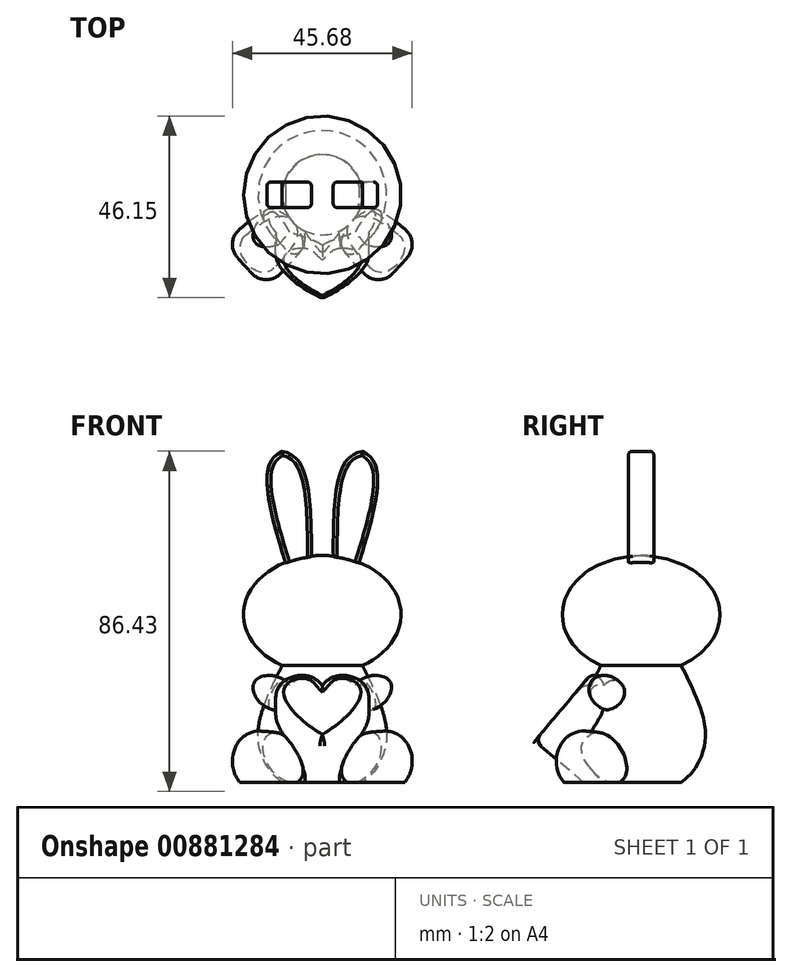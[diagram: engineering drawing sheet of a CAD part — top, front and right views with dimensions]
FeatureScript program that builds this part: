
annotation { "Feature Type Name" : "Feature", "Feature Type Description" : "" }
export const myFeature = defineFeature(function(context is Context, id is Id, definition is map)
    precondition{}
    {
        {
            var Q0;
            Q0=qCreatedBy(makeId("Front.planeOp"),FACE);
            var sketch = newSketch(context, id + "F0", { "sketchPlane" : qUnion([Q0])});
            skEllipticalArc(sketch, "E0", {});
            skLineSegment(sketch, "E1", {"start": v(0, 24.54) * mm, "end": v(0, -22.96) * mm, "construction": true});
            skLineSegment(sketch, "E2", {"start": v(0, 15) * mm, "end": v(0, -15) * mm});
            const initialGuessF0  = {"E0": [0, 0, -1, 0, 0.02, 0.015, 4.71238898038469, 1.5707963267948966]};
            skSetInitialGuess(sketch, initialGuessF0);
            skSolve(sketch);
        }
        {
            var Q0;
            Q0=makeQuery(id+"F0.imprint","IMPRINT",FACE,{"disambiguationData":[TD([[makeQuery(id+"F0.imprint","IMPRINT",EDGE,{"derivedFrom":sQuery(id+"F0.wireOp",EDGE,"E0")}),1.0]])]});
            var Q1;
            Q1=sQuery(id+"F0.wireOp",EDGE,"E1");
            revolve(context, id + "F1", {"surfaceOperationType" : NewSurfaceOperationType.NEW, "entities" : qUnion([Q0]), "axis" : qUnion([Q1]), "revolveType" : RevolveType.FULL});
        }
        {
            var Q0;
            Q0=qCreatedBy(makeId("Front.planeOp"),FACE);
            var sketch = newSketch(context, id + "F2", { "sketchPlane" : qUnion([Q0])});
            skLineSegment(sketch, "E3", {"start": v(-4, 0) * mm, "end": v(-10.24, 41.49) * mm, "construction": true});
            skLineSegment(sketch, "E4", {"start": v(-4, 0) * mm, "end": v(-4, 44.56) * mm, "construction": true});
            skFitSpline(sketch, "E5", {"points": [v(-8.8, 11.5) * mm, v(-13.75, 30.32) * mm, v(-13.13, 38.8) * mm, v(-10.24, 41.49) * mm], "startDerivative": vector(-13.36, 42.4) * mm, "endDerivative": vector(15.53, 10.02) * mm});
            skFitSpline(sketch, "E6.MirrorCS", {"points": [v(-2.8, 12.4) * mm, v(-3.6, 31.85) * mm, v(-6.68, 39.77) * mm, v(-10.24, 41.49) * mm], "startDerivative": vector(0.3, 44.46) * mm, "endDerivative": vector(-17.79, 5) * mm});
            skLineSegment(sketch, "E7", {"start": v(-8.8, 11.5) * mm, "end": v(-2.8, 12.4) * mm});
            skSolve(sketch);
        }
        {
            var Q0;
            {var subQ5=sQuery(id+"F2.wireOp",EDGE,"E5");Q0=makeQuery(id+"F2.imprint","IMPRINT",FACE,{"disambiguationData":[TD([[makeQuery(id+"F2.imprint","IMPRINT",EDGE,{"derivedFrom":subQ5}),-1.0]])]});}
            extrude(context, id + "F3", {"entities" : qUnion([Q0]), "operationType" : NewBodyOperationType.ADD, "endBound" : BoundingType.SYMMETRIC, "depth" : 6.5 * mm, "offsetDistance" : 25 * mm});
        }
        {
            var Q0;
            Q0=makeQuery(id+"F3.opExtrude","CAP_EDGE",EDGE,{"disambiguationData":[OSD([sQuery(id+"F2.wireOp",EDGE,"E5")])],"isStart":true});
            var Q1;
            Q1=makeQuery(id+"F3.opExtrude","CAP_EDGE",EDGE,{"disambiguationData":[OSD([sQuery(id+"F2.wireOp",EDGE,"E5")])],"isStart":false});
            var Q2;
            Q2=makeQuery(id+"F3.opExtrude","CAP_EDGE",EDGE,{"disambiguationData":[OSD([sQuery(id+"F2.wireOp",EDGE,"E6.MirrorCS")])],"isStart":false});
            var Q3;
            {var subQ0=sQuery(id+"F2.wireOp",EDGE,"E6.MirrorCS");var subQ1=sQuery(id+"F2.wireOp",EDGE,"E5");Q3=makeQuery(id+"FyARzWtpv3hHTZw_1.opFillet","BLEND_EDGE",EDGE,{"blendedFrom":[makeQuery(id+"F3.opExtrude","SWEPT_EDGE",EDGE,{"disambiguationData":[OSD([subQ1,subQ0])]}),makeQuery(id+"F3.opExtrude","CAP_FACE",FACE,{"disambiguationData":[OSD([subQ1,subQ0,sQuery(id+"F2.wireOp",EDGE,"E7")])],"isStart":false})],"blendedInto":[makeQuery(id+"F3.opExtrude","CAP_FACE",FACE,{"disambiguationData":[OSD([subQ1,subQ0,sQuery(id+"F2.wireOp",EDGE,"E7")])],"isStart":false})]});}
            var Q4;
            {var subQ0=sQuery(id+"F2.wireOp",EDGE,"E6.MirrorCS");var subQ1=sQuery(id+"F2.wireOp",EDGE,"E5");Q4=makeQuery(id+"FyARzWtpv3hHTZw_1.opFillet","BLEND_EDGE",EDGE,{"blendedFrom":[makeQuery(id+"F3.opExtrude","SWEPT_EDGE",EDGE,{"disambiguationData":[OSD([subQ1,subQ0])]}),makeQuery(id+"F3.opExtrude","CAP_FACE",FACE,{"disambiguationData":[OSD([subQ1,subQ0,sQuery(id+"F2.wireOp",EDGE,"E7")])],"isStart":true})],"blendedInto":[makeQuery(id+"F3.opExtrude","CAP_FACE",FACE,{"disambiguationData":[OSD([subQ1,subQ0,sQuery(id+"F2.wireOp",EDGE,"E7")])],"isStart":true})]});}
            var Q5;
            Q5=makeQuery(id+"F3.opExtrude","CAP_EDGE",EDGE,{"disambiguationData":[OSD([sQuery(id+"F2.wireOp",EDGE,"E6.MirrorCS")])],"isStart":true});
            fillet(context, id + "F4", {"entities" : qUnion([Q0, Q1, Q2, Q3, Q4, Q5]), "radius" : 1 * mm, "tangentPropagation" : true, "allowEdgeOverflow" : false});
        }
        {
            var Q0;
            Q0=qCreatedBy(makeId("Front.planeOp"),FACE);
            var sketch = newSketch(context, id + "F5", { "sketchPlane" : qUnion([Q0])});
            skFitSpline(sketch, "E8", {"points": [v(-9.33, -11.24) * mm, v(-15.1, -23.9) * mm, v(-16.02, -33.64) * mm, v(-4.18, -45.01) * mm], "startDerivative": vector(-24.57, -48.49) * mm, "endDerivative": vector(60.2, -10.38) * mm});
            skLineSegment(sketch, "E9", {"start": v(-9.33, -11.24) * mm, "end": v(0, -11.24) * mm});
            skLineSegment(sketch, "E10", {"start": v(-4.18, -45.01) * mm, "end": v(0, -45.01) * mm});
            skLineSegment(sketch, "E11", {"start": v(0, -11.24) * mm, "end": v(0, -45.01) * mm});
            skSolve(sketch);
        }
        {
            var Q0;
            Q0=makeQuery(id+"F5.imprint","IMPRINT",FACE,{"disambiguationData":[TD([[makeQuery(id+"F5.imprint","IMPRINT",EDGE,{"derivedFrom":sQuery(id+"F5.wireOp",EDGE,"E8")}),1.0]])]});
            var Q1;
            Q1=sQuery(id+"F5.wireOp",EDGE,"E11");
            revolve(context, id + "F6", {"operationType" : NewBodyOperationType.ADD, "surfaceOperationType" : NewSurfaceOperationType.NEW, "entities" : qUnion([Q0]), "axis" : qUnion([Q1]), "revolveType" : RevolveType.FULL});
        }
        {
            var Q0;
            Q0=qCreatedBy(makeId("Front.planeOp"),FACE);
            var sketch = newSketch(context, id + "F7", { "sketchPlane" : qUnion([Q0])});
            skLineSegment(sketch, "E12", {"start": v(0, 66.85) * mm, "end": v(0, -35.64) * mm});
            skSolve(sketch);
        }
        {
            var Q0;
            Q0=qCreatedBy(makeId("Right.planeOp"),FACE);
            var Q1;
            Q1=sQuery(id+"F7.wireOp",EDGE,"E12");
            cPlane(context, id + "F8", {"entities" : qUnion([Q0, Q1]), "cplaneType" : CPlaneType.LINE_ANGLE, "offset" : 25 * mm, "angle" : 55 * degree, "width" : 150 * mm, "height" : 150 * mm});
        }
        {
            var Q0;
            Q0=qCreatedBy(id+"F8.planeOp",FACE);
            var sketch = newSketch(context, id + "F9", { "sketchPlane" : qUnion([Q0])});
            skLineSegment(sketch, "E13", {"start": v(0, -26.37) * mm, "end": v(20.72, -17.4) * mm, "construction": true});
            skFitSpline(sketch, "E14", {"points": [v(20.72, -17.4) * mm, v(17.52, -15.54) * mm, v(13.38, -16.1) * mm, v(6.63, -21.37) * mm], "startDerivative": vector(-5.3, 12.6) * mm, "endDerivative": vector(-15.78, -18.55) * mm});
            skLineSegment(sketch, "E15", {"start": v(6.63, -21.37) * mm, "end": v(7.4, -23.17) * mm});
            skLineSegment(sketch, "E16", {"start": v(7.4, -23.17) * mm, "end": v(20.72, -17.4) * mm});
            skSolve(sketch);
        }
        {
            var Q0;
            Q0=makeQuery(id+"F9.imprint","IMPRINT",FACE,{"disambiguationData":[TD([[makeQuery(id+"F9.imprint","IMPRINT",EDGE,{"derivedFrom":sQuery(id+"F9.wireOp",EDGE,"E14")}),1.0]])]});
            var Q1;
            Q1=sQuery(id+"F9.wireOp",EDGE,"E13");
            revolve(context, id + "F10", {"operationType" : NewBodyOperationType.ADD, "surfaceOperationType" : NewSurfaceOperationType.NEW, "entities" : qUnion([Q0]), "axis" : qUnion([Q1]), "revolveType" : RevolveType.FULL});
        }
        {
            var Q0;
            Q0=qCreatedBy(makeId("Right.planeOp"),FACE);
            var Q1;
            Q1=sQuery(id+"F7.wireOp",EDGE,"E12");
            cPlane(context, id + "F11", {"entities" : qUnion([Q0, Q1]), "cplaneType" : CPlaneType.LINE_ANGLE, "offset" : 25 * mm, "angle" : 47.74 * degree, "width" : 150 * mm, "height" : 150 * mm});
        }
        {
            var Q0;
            Q0=qCreatedBy(id+"F11.planeOp",FACE);
            var sketch = newSketch(context, id + "F12", { "sketchPlane" : qUnion([Q0])});
            skLineSegment(sketch, "E17", {"start": v(-1.93, -45.01) * mm, "end": v(26.68, -45.01) * mm, "construction": true});
            skLineSegment(sketch, "E18", {"start": v(4.34, -37.27) * mm, "end": v(26.68, -37.27) * mm});
            skFitSpline(sketch, "E19", {"points": [v(26.68, -45.01) * mm, v(11.79, -43.58) * mm, v(7.97, -41.17) * mm, v(4.34, -37.27) * mm], "startDerivative": vector(-45.37, 0) * mm, "endDerivative": vector(-2.7, 18.32) * mm});
            skLineSegment(sketch, "E20", {"start": v(26.68, -37.27) * mm, "end": v(26.68, -45.01) * mm});
            skSolve(sketch);
        }
        {
            var Q0;
            Q0=makeQuery(id+"F12.imprint","IMPRINT",FACE,{"disambiguationData":[TD([[makeQuery(id+"F12.imprint","IMPRINT",EDGE,{"derivedFrom":sQuery(id+"F12.wireOp",EDGE,"E18")}),-1.0]])]});
            var Q1;
            Q1=sQuery(id+"F12.wireOp",EDGE,"E18");
            revolve(context, id + "F13", {"operationType" : NewBodyOperationType.ADD, "surfaceOperationType" : NewSurfaceOperationType.NEW, "entities" : qUnion([Q0]), "axis" : qUnion([Q1]), "revolveType" : RevolveType.FULL});
        }
        {
            var Q0;
            Q0=makeQuery(id+"F13.opRevolve","SWEPT_FACE",FACE,{"disambiguationData":[OSD([sQuery(id+"F12.wireOp",EDGE,"E20")])]});
            fillet(context, id + "F14", {"entities" : qUnion([Q0]), "radius" : 5 * mm, "tangentPropagation" : true, "allowEdgeOverflow" : false});
        }
        {
            var Q0;
            Q0=makeQuery(id+"F1.opRevolve","SWEPT_BODY",BODY,{"disambiguationData":[OSD([sQuery(id+"F0.wireOp",EDGE,"E0"),sQuery(id+"F0.wireOp",EDGE,"E2")])]});
            var Q1;
            Q1=qCreatedBy(makeId("Right.planeOp"),FACE);
            mirror(context, id + "F15", {"operationType" : NewBodyOperationType.ADD, "entities" : qUnion([Q0]), "mirrorPlane" : qUnion([Q1])});
        }
        {
            var Q0;
            Q0=qCreatedBy(makeId("Right.planeOp"),FACE);
            var sketch = newSketch(context, id + "F16", { "sketchPlane" : qUnion([Q0])});
            skLineSegment(sketch, "E21.bottom", {"start": v(-62.98, -42.6) * mm, "end": v(55.22, -42.6) * mm});
            skLineSegment(sketch, "E21.top", {"start": v(-62.98, -59.08) * mm, "end": v(55.22, -59.08) * mm});
            skLineSegment(sketch, "E21.left", {"start": v(-62.98, -42.6) * mm, "end": v(-62.98, -59.08) * mm});
            skLineSegment(sketch, "E21.right", {"start": v(55.22, -42.6) * mm, "end": v(55.22, -59.08) * mm});
            skSolve(sketch);
        }
        {
            var Q0;
            Q0=qCreatedBy(makeId("Front.planeOp"),FACE);
            var sketch = newSketch(context, id + "F17", { "sketchPlane" : qUnion([Q0])});
            skLineSegment(sketch, "E22", {"start": v(-76.04, 0) * mm, "end": v(112.93, 0) * mm});
            skSolve(sketch);
        }
        {
            var Q0;
            Q0=qCreatedBy(makeId("Front.planeOp"),FACE);
            var Q1;
            Q1=sQuery(id+"F17.wireOp",EDGE,"E22");
            cPlane(context, id + "F18", {"entities" : qUnion([Q0, Q1]), "cplaneType" : CPlaneType.LINE_ANGLE, "offset" : 25 * mm, "angle" : 40 * degree, "oppositeDirection" : true, "width" : 150 * mm, "height" : 150 * mm});
        }
        {
            var Q0;
            Q0=qCreatedBy(id+"F18.planeOp",FACE);
            var sketch = newSketch(context, id + "F19", { "sketchPlane" : qUnion([Q0])});
            skFitSpline(sketch, "E23", {"points": [v(0, -22.26) * mm, v(8.35, -19.9) * mm, v(11.56, -23.82) * mm, v(11.07, -29.37) * mm, v(0, -42.26) * mm], "startDerivative": vector(28, 44.66) * mm, "endDerivative": vector(-50.83, -35.83) * mm});
            skFitSpline(sketch, "E24.MirrorCS", {"points": [v(0, -22.26) * mm, v(-8.35, -19.9) * mm, v(-11.56, -23.82) * mm, v(-11.07, -29.37) * mm, v(0, -42.26) * mm], "startDerivative": vector(-28, 44.66) * mm, "endDerivative": vector(50.83, -35.83) * mm});
            skSolve(sketch);
        }
        {
            var Q0;
            Q0=makeQuery(id+"F19.imprint","IMPRINT",FACE,{"disambiguationData":[TD([[makeQuery(id+"F19.imprint","IMPRINT",EDGE,{"derivedFrom":sQuery(id+"F19.wireOp",EDGE,"E23")}),-1.0]])]});
            extrude(context, id + "F20", {"entities" : qUnion([Q0]), "operationType" : NewBodyOperationType.ADD, "depth" : 21.2 * mm, "offsetDistance" : 25 * mm});
        }
        {
            var Q0;
            Q0=makeQuery(id+"F20.opExtrude","CAP_FACE",FACE,{"disambiguationData":[OSD([sQuery(id+"F19.wireOp",EDGE,"E23"),sQuery(id+"F19.wireOp",EDGE,"E24.MirrorCS")])],"isStart":true});
            fillet(context, id + "F21", {"entities" : qUnion([Q0]), "radius" : 2 * mm, "tangentPropagation" : true, "allowEdgeOverflow" : false});
        }
        {
            var Q0;
            {var subQ0=sQuery(id+"F19.wireOp",EDGE,"E24.MirrorCS");var subQ1=sQuery(id+"F19.wireOp",EDGE,"E23");Q0=makeQuery(id+"F20.opExtrude","SWEPT_EDGE",EDGE,{"disambiguationData":[OSD([subQ1,subQ0]),TDD([makeQuery(id+"F19.imprint","INTERSECT",VERTEX,{"disambiguationData":[OD(1.0)],"derivedFrom":[subQ1,subQ0]})])]});}
            fillet(context, id + "F22", {"entities" : qUnion([Q0]), "radius" : 1 * mm, "tangentPropagation" : true, "allowEdgeOverflow" : false});
        }
        {
            var Q0;
            Q0=makeQuery(id+"F16.imprint","IMPRINT",FACE,{"disambiguationData":[TD([[makeQuery(id+"F16.imprint","IMPRINT",EDGE,{"derivedFrom":sQuery(id+"F16.wireOp",EDGE,"E21.bottom")}),-1.0]])]});
            extrude(context, id + "F23", {"entities" : qUnion([Q0]), "operationType" : NewBodyOperationType.REMOVE, "endBound" : BoundingType.SYMMETRIC, "oppositeDirection" : true, "depth" : 110.8 * mm, "offsetDistance" : 25 * mm});
        }
    });
